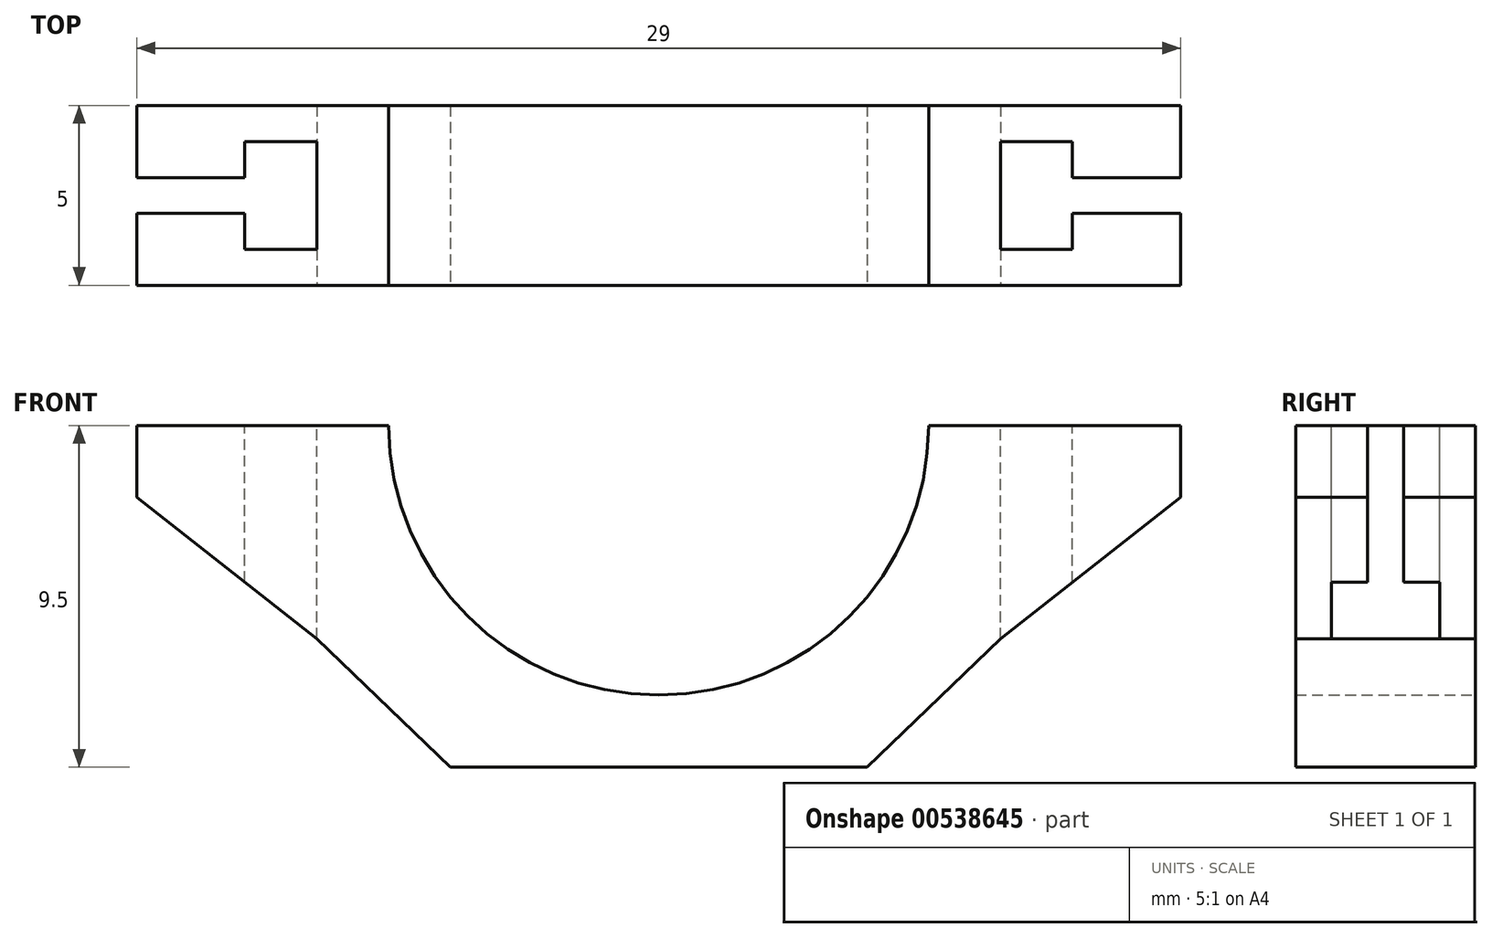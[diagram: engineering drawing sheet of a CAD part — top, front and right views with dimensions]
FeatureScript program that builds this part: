
annotation { "Feature Type Name" : "Feature", "Feature Type Description" : "" }
export const myFeature = defineFeature(function(context is Context, id is Id, definition is map)
    precondition{}
    {
        {
            var Q0;
            Q0=qCreatedBy(makeId("Front.planeOp"),FACE);
            var sketch = newSketch(context, id + "F0", { "sketchPlane" : qUnion([Q0])});
            skArc(sketch, "E0", {"start": v(-8.75, 0) * mm, "mid": v(-1.25, -7.5) * mm, "end": v(6.25, 0) * mm});
            skArc(sketch, "E1", {"start": v(-10.75, 0) * mm, "mid": v(-1.25, -9.5) * mm, "end": v(8.25, 0) * mm});
            skLineSegment(sketch, "E2", {"start": v(-10.75, 0) * mm, "end": v(-8.75, 0) * mm});
            skLineSegment(sketch, "E3", {"start": v(6.25, 0) * mm, "end": v(8.25, 0) * mm});
            skLineSegment(sketch, "E4.top", {"start": v(-10.75, -9.5) * mm, "end": v(8.25, -9.5) * mm});
            skLineSegment(sketch, "E4.left", {"start": v(-10.75, 0) * mm, "end": v(-10.75, -9.5) * mm});
            skLineSegment(sketch, "E4.right", {"start": v(8.25, 0) * mm, "end": v(8.25, -9.5) * mm});
            skLineSegment(sketch, "E5", {"start": v(8.25, 0) * mm, "end": v(13.25, 0) * mm});
            skLineSegment(sketch, "E6", {"start": v(13.25, 0) * mm, "end": v(13.25, -2) * mm});
            skLineSegment(sketch, "E7", {"start": v(13.25, -2) * mm, "end": v(8.25, -2) * mm});
            skLineSegment(sketch, "E8", {"start": v(-10.75, 0) * mm, "end": v(-15.75, 0) * mm});
            skLineSegment(sketch, "E9", {"start": v(-15.75, 0) * mm, "end": v(-15.75, -2) * mm});
            skLineSegment(sketch, "E10", {"start": v(-15.75, -2) * mm, "end": v(-10.75, -2) * mm});
            skSolve(sketch);
        }
        {
            var Q0;
            Q0=qSketchRegion(id+"F0",true);
            extrude(context, id + "F1", {"entities" : qUnion([Q0]), "endBound" : BoundingType.SYMMETRIC, "depth" : 5 * mm, "offsetDistance" : 25 * mm});
        }
        {
            var Q0;
            Q0=qCreatedBy(makeId("Top.planeOp"),FACE);
            var sketch = newSketch(context, id + "F2", { "sketchPlane" : qUnion([Q0])});
            skLineSegment(sketch, "E11", {"start": v(-15.75, 0) * mm, "end": v(13.25, 0) * mm, "construction": true});
            skLineSegment(sketch, "E12", {"start": v(-1.25, 2.7) * mm, "end": v(-1.25, -2.7) * mm, "construction": true});
            skPoint(sketch, "E12.startSnap0", {"position": v(-1.25, 0) * mm});
            skSolve(sketch);
        }
        {
            var Q0;
            Q0=makeQuery(id+"FPUExMqadZdAYgq_1.boolean.opBoolean","MERGE",FACE,{"derivedFrom":[makeQuery(id+"F1.opExtrude","SWEPT_FACE",FACE,{"disambiguationData":[OSD([sQuery(id+"F0.wireOp",EDGE,"E4.right")])]}),makeQuery(id+"FPUExMqadZdAYgq_1.opExtrude","SWEPT_FACE",FACE,{"disambiguationData":[OSD([sQuery(id+"F6.wireOp",EDGE,"E41.MirrorCS")])]})]});
            var sketch = newSketch(context, id + "F3", { "sketchPlane" : qUnion([Q0])});
            skLineSegment(sketch, "E13", {"start": v(5.18, -9.5) * mm, "end": v(-2.5, -9.5) * mm, "construction": true});
            skLineSegment(sketch, "E14", {"start": v(-2.5, -9.5) * mm, "end": v(12.55, -5.47) * mm, "construction": true});
            skLineSegment(sketch, "E15", {"start": v(2.5, -8.16) * mm, "end": v(2.5, -9.5) * mm});
            skLineSegment(sketch, "E16", {"start": v(2.5, -8.16) * mm, "end": v(-2.5, -9.5) * mm});
            skLineSegment(sketch, "E17", {"start": v(-2.5, -9.5) * mm, "end": v(2.5, -9.5) * mm});
            skSolve(sketch);
        }
        {
            var Q0;
            Q0=makeQuery(id+"F1.opExtrude","CAP_FACE",FACE,{"disambiguationData":[OSD([sQuery(id+"F0.wireOp",EDGE,"E0"),sQuery(id+"F0.wireOp",EDGE,"E2"),sQuery(id+"F0.wireOp",EDGE,"E4.top"),sQuery(id+"F0.wireOp",EDGE,"E4.left"),sQuery(id+"F0.wireOp",EDGE,"E4.right"),sQuery(id+"F0.wireOp",EDGE,"E3"),sQuery(id+"F0.wireOp",EDGE,"E5"),sQuery(id+"F0.wireOp",EDGE,"E6"),sQuery(id+"F0.wireOp",EDGE,"E7"),sQuery(id+"F0.wireOp",EDGE,"E8"),sQuery(id+"F0.wireOp",EDGE,"E9"),sQuery(id+"F0.wireOp",EDGE,"E10")])],"isStart":false});
            var sketch = newSketch(context, id + "F4", { "sketchPlane" : qUnion([Q0])});
            skLineSegment(sketch, "E18", {"start": v(-1.25, -9.5) * mm, "end": v(-1.25, -7.5) * mm, "construction": true});
            skLineSegment(sketch, "E19", {"start": v(8.25, -2) * mm, "end": v(8.25, 0) * mm, "construction": true});
            skLineSegment(sketch, "E20", {"start": v(-10.75, -2) * mm, "end": v(-10.75, 0) * mm, "construction": true});
            skLineSegment(sketch, "E21", {"start": v(-8.75, -7.5) * mm, "end": v(6.25, -7.5) * mm, "construction": true});
            skLineSegment(sketch, "E22", {"start": v(6.25, 0) * mm, "end": v(6.25, -7.5) * mm, "construction": true});
            skLineSegment(sketch, "E23", {"start": v(-8.75, 0) * mm, "end": v(-8.75, -7.5) * mm, "construction": true});
            skPoint(sketch, "E24.start.orphan", {"position": v(13.25, -2) * mm});
            skPoint(sketch, "E25.MirrorCS.start.orphan", {"position": v(-15.75, -2) * mm});
            skPoint(sketch, "E26", {"position": v(6.25, -7.5) * mm});
            skLineSegment(sketch, "E27", {"start": v(13.25, -2) * mm, "end": v(6.25, -7.5) * mm});
            skLineSegment(sketch, "E28.MirrorCS", {"start": v(-15.75, -2) * mm, "end": v(-8.75, -7.5) * mm});
            skPoint(sketch, "E29.orphan", {"position": v(-10.75, -7.5) * mm});
            skPoint(sketch, "E30.end.orphan", {"position": v(-8.75, -9.5) * mm});
            skPoint(sketch, "E31.end.orphan", {"position": v(6.25, -9.5) * mm});
            skPoint(sketch, "E32", {"position": v(-8.05, -9.5) * mm});
            skPoint(sketch, "E33.MirrorP", {"position": v(5.55, -9.5) * mm});
            skLineSegment(sketch, "E34", {"start": v(-8.75, -7.5) * mm, "end": v(-8.05, -9.5) * mm});
            skLineSegment(sketch, "E35", {"start": v(6.25, -7.5) * mm, "end": v(5.55, -9.5) * mm});
            skSolve(sketch);
        }
        {
            var Q0;
            {var subQ1=makeQuery(id+"F1.opExtrude","CAP_EDGE",EDGE,{"disambiguationData":[OSD([sQuery(id+"F0.wireOp",EDGE,"E10")])],"isStart":false});Q0=makeQuery(id+"F4.imprint","IMPRINT",FACE,{"disambiguationData":[TD([[makeQuery(id+"F4.imprint","IMPRINT",EDGE,{"derivedFrom":subQ1}),-1.0]])]});}
            var Q1;
            {var subQ1=makeQuery(id+"F1.opExtrude","CAP_EDGE",EDGE,{"disambiguationData":[OSD([sQuery(id+"F0.wireOp",EDGE,"E7")])],"isStart":false});Q1=makeQuery(id+"F4.imprint","IMPRINT",FACE,{"disambiguationData":[TD([[makeQuery(id+"F4.imprint","IMPRINT",EDGE,{"derivedFrom":subQ1}),1.0]])]});}
            var Q2;
            Q2=makeQuery(id+"F1.opExtrude","CAP_FACE",FACE,{"disambiguationData":[OSD([sQuery(id+"F0.wireOp",EDGE,"E0"),sQuery(id+"F0.wireOp",EDGE,"E2"),sQuery(id+"F0.wireOp",EDGE,"E4.top"),sQuery(id+"F0.wireOp",EDGE,"E4.left"),sQuery(id+"F0.wireOp",EDGE,"E4.right"),sQuery(id+"F0.wireOp",EDGE,"E3"),sQuery(id+"F0.wireOp",EDGE,"E5"),sQuery(id+"F0.wireOp",EDGE,"E6"),sQuery(id+"F0.wireOp",EDGE,"E7"),sQuery(id+"F0.wireOp",EDGE,"E8"),sQuery(id+"F0.wireOp",EDGE,"E9"),sQuery(id+"F0.wireOp",EDGE,"E10")])],"isStart":true});
            extrude(context, id + "F5", {"entities" : qUnion([Q0, Q1]), "operationType" : NewBodyOperationType.ADD, "endBound" : BoundingType.UP_TO_SURFACE, "oppositeDirection" : true, "depth" : 25 * mm, "endBoundEntityFace" : qUnion([Q2]), "offsetDistance" : 25 * mm});
        }
        {
            var Q0;
            Q0=makeQuery(id+"F1.opExtrude","SWEPT_FACE",FACE,{"disambiguationData":[OSD([sQuery(id+"F0.wireOp",EDGE,"E3"),sQuery(id+"F0.wireOp",EDGE,"E5")])]});
            var sketch = newSketch(context, id + "F6", { "sketchPlane" : qUnion([Q0])});
            skLineSegment(sketch, "E36.bottom", {"start": v(-15.75, 0.5) * mm, "end": v(-10.75, 0.5) * mm});
            skLineSegment(sketch, "E36.top", {"start": v(-15.75, -0.5) * mm, "end": v(-10.75, -0.5) * mm});
            skLineSegment(sketch, "E36.left", {"start": v(-15.75, 0.5) * mm, "end": v(-15.75, -0.5) * mm});
            skLineSegment(sketch, "E36.right", {"start": v(-10.75, 0.5) * mm, "end": v(-10.75, -0.5) * mm});
            skPoint(sketch, "E37", {"position": v(-15.75, 0) * mm});
            skLineSegment(sketch, "E38.bottom", {"start": v(-12.75, 1.5) * mm, "end": v(-10.75, 1.5) * mm});
            skLineSegment(sketch, "E38.top", {"start": v(-12.75, -1.5) * mm, "end": v(-10.75, -1.5) * mm});
            skLineSegment(sketch, "E38.left", {"start": v(-12.75, 1.5) * mm, "end": v(-12.75, -1.5) * mm});
            skLineSegment(sketch, "E38.right", {"start": v(-10.75, 1.5) * mm, "end": v(-10.75, -1.5) * mm});
            skPoint(sketch, "E38.middle", {"position": v(-11.75, 0) * mm});
            skLineSegment(sketch, "E39.MirrorCS", {"start": v(13.25, 0.5) * mm, "end": v(13.25, -0.5) * mm});
            skPoint(sketch, "E40.MirrorP", {"position": v(7, 0) * mm});
            skLineSegment(sketch, "E41.MirrorCS", {"start": v(8.25, 1.5) * mm, "end": v(8.25, -1.5) * mm});
            skLineSegment(sketch, "E42.MirrorCS", {"start": v(10.25, 1.5) * mm, "end": v(10.25, 0.5) * mm});
            skLineSegment(sketch, "E43.MirrorCS", {"start": v(10.25, -1.5) * mm, "end": v(8.25, -1.5) * mm});
            skPoint(sketch, "E44.MirrorP", {"position": v(3, 0) * mm});
            skLineSegment(sketch, "E45.MirrorCS", {"start": v(10.25, 1.5) * mm, "end": v(8.25, 1.5) * mm});
            skLineSegment(sketch, "E46.MirrorCS", {"start": v(13.25, -0.5) * mm, "end": v(10.25, -0.5) * mm});
            skLineSegment(sketch, "E47.MirrorCS", {"start": v(13.25, 0.5) * mm, "end": v(10.25, 0.5) * mm});
            skLineSegment(sketch, "E48.trimOffspring", {"start": v(10.25, -0.5) * mm, "end": v(10.25, -1.5) * mm});
            skSolve(sketch);
        }
        {
            var Q0;
            Q0 = qSketchRegion(id + "F6", true);
            extrude(context, id + "F7", {"entities" : qUnion([Q0]), "operationType" : NewBodyOperationType.REMOVE, "oppositeDirection" : true, "depth" : 25 * mm, "offsetDistance" : 25 * mm});
        }
        {
            var Q0;
            Q0=makeQuery(id+"F3.imprint","IMPRINT",FACE,{"disambiguationData":[TD([[makeQuery(id+"F3.imprint","IMPRINT",EDGE,{"derivedFrom":sQuery(id+"F3.wireOp",EDGE,"E15")}),-1.0]])]});
            extrude(context, id + "F8", {"entities" : qUnion([Q0]), "operationType" : NewBodyOperationType.REMOVE, "oppositeDirection" : true, "depth" : 25 * mm, "offsetDistance" : 25 * mm});
        }
        {
            var Q0;
            Q0=makeQuery(id+"F3.imprint","IMPRINT",FACE,{"disambiguationData":[TD([[makeQuery(id+"F3.imprint","IMPRINT",EDGE,{"derivedFrom":sQuery(id+"F3.wireOp",EDGE,"E15")}),-1.0]])]});
            var Q1;
            Q1=makeQuery(id+"F7.boolean.opBoolean","MERGE",FACE,{"derivedFrom":[makeQuery(id+"F1.opExtrude","SWEPT_FACE",FACE,{"disambiguationData":[OSD([sQuery(id+"F0.wireOp",EDGE,"E4.left")])]}),makeQuery(id+"F7.opExtrude","SWEPT_FACE",FACE,{"disambiguationData":[OSD([sQuery(id+"F6.wireOp",EDGE,"E38.right")])]})]});
            extrude(context, id + "F9", {"entities" : qUnion([Q0]), "operationType" : NewBodyOperationType.ADD, "endBound" : BoundingType.UP_TO_SURFACE, "oppositeDirection" : true, "depth" : 25 * mm, "endBoundEntityFace" : qUnion([Q1]), "offsetDistance" : 25 * mm});
        }
        {
            var Q0;
            {var subQ5=sQuery(id+"F4.wireOp",EDGE,"E34");Q0=makeQuery(id+"F4.imprint","IMPRINT",FACE,{"disambiguationData":[TD([[makeQuery(id+"F4.imprint","IMPRINT",EDGE,{"derivedFrom":subQ5}),1.0]])]});}
            var sketch = newSketch(context, id + "F10", { "sketchPlane" : qUnion([Q0])});
            skPoint(sketch, "E49", {"position": v(4.54, -9.5) * mm});
            skPoint(sketch, "E50.MirrorP", {"position": v(-7.04, -9.5) * mm});
            skLineSegment(sketch, "E51", {"start": v(-7.04, -9.5) * mm, "end": v(-10.75, -5.93) * mm});
            skLineSegment(sketch, "E52", {"start": v(-10.75, -5.93) * mm, "end": v(-10.75, -9.5) * mm});
            skLineSegment(sketch, "E53", {"start": v(-10.75, -9.5) * mm, "end": v(-7.04, -9.5) * mm});
            skLineSegment(sketch, "E54.MirrorCS", {"start": v(4.54, -9.5) * mm, "end": v(8.25, -5.93) * mm});
            skLineSegment(sketch, "E55.MirrorCS", {"start": v(8.25, -9.5) * mm, "end": v(4.54, -9.5) * mm});
            skLineSegment(sketch, "E56.MirrorCS", {"start": v(8.25, -5.93) * mm, "end": v(8.25, -9.5) * mm});
            skSolve(sketch);
        }
        {
            var Q0;
            Q0 = qSketchRegion(id + "F10", true);
            extrude(context, id + "F11", {"entities" : qUnion([Q0]), "operationType" : NewBodyOperationType.REMOVE, "oppositeDirection" : true, "depth" : 25 * mm, "offsetDistance" : 25 * mm});
        }
    });
